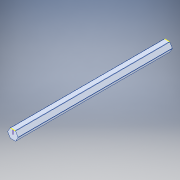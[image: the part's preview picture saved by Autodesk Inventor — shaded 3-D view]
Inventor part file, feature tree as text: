
AUTODESK INVENTOR PART (.ipt)
format: ipt  version: 2017 (Build 210142000, 142)  size: 133,120 bytes
history: native  units: in
note: dims shown in document units (in); Inventor stores cm internally (conversion verified against a paired STEP export)
features: sketch x3, split x1, fillet x1
ambient origin geometry x8: Origin, YZ Plane, XZ Plane, XY Plane, X Axis, Y Axis, Z Axis, Center Point
bodies: Solid1 (feature_tree)
feature tree (5):
  split  "Split1"
  sketch  "Sketch2"
  sketch  "Sketch3"
  sketch  "Sketch1"
  fillet  "Fillet1"  Radius=8.5in
